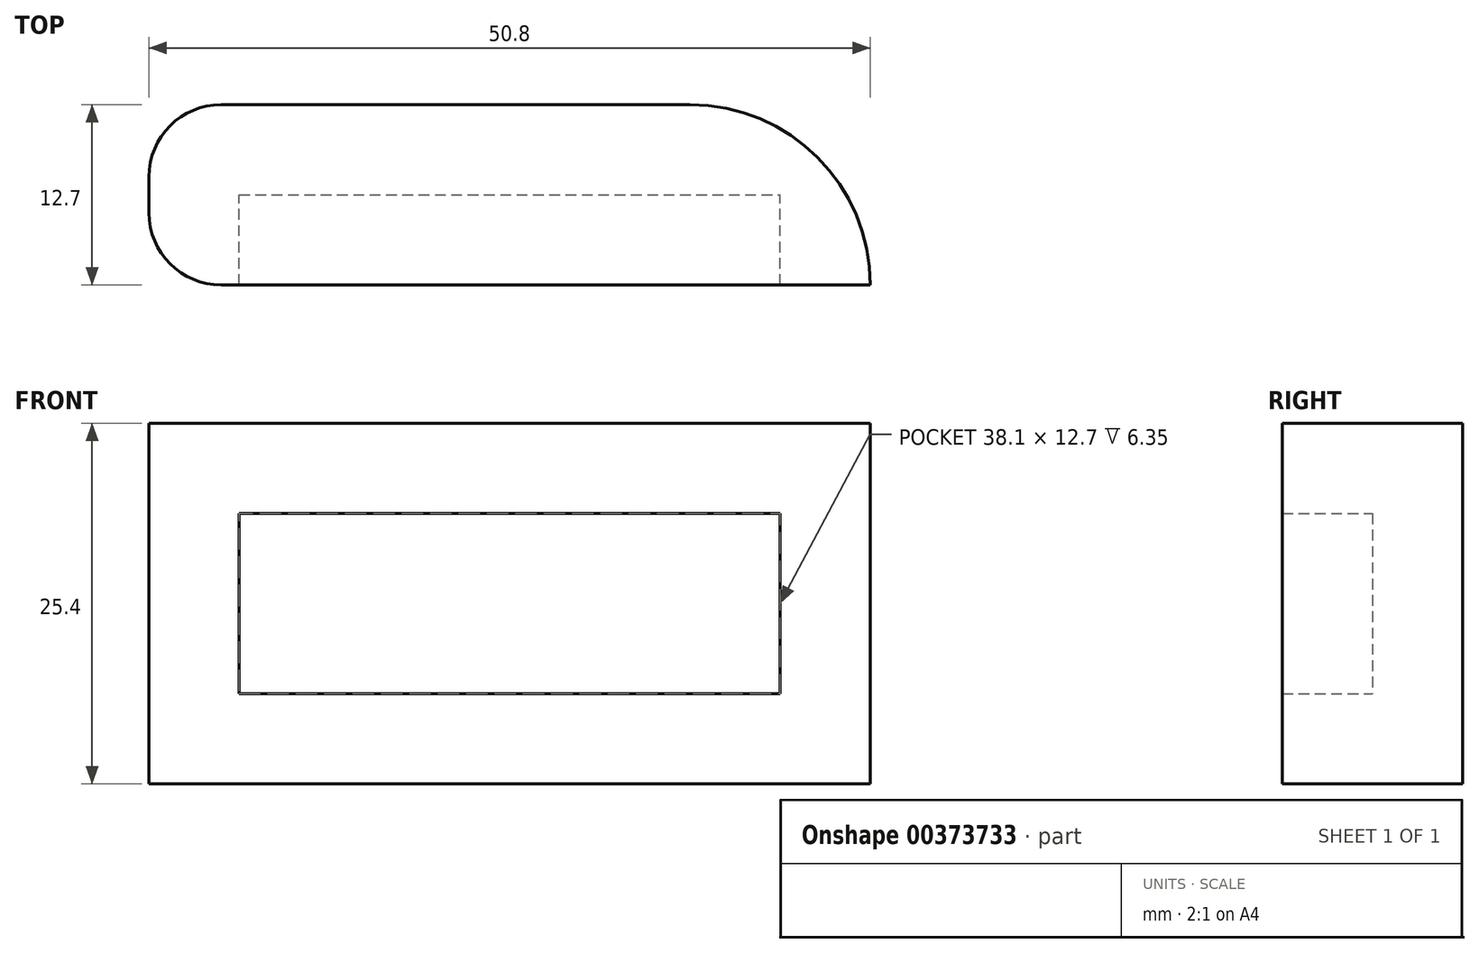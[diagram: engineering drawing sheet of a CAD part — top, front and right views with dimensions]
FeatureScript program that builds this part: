
annotation { "Feature Type Name" : "Feature", "Feature Type Description" : "" }
export const myFeature = defineFeature(function(context is Context, id is Id, definition is map)
    precondition{}
    {
        {
            var Q0;
            Q0=qCreatedBy(makeId("Front.planeOp"),FACE);
            var sketch = newSketch(context, id + "F0", { "sketchPlane" : qUnion([Q0])});
            skLineSegment(sketch, "E0.bottom", {"start": v(0, 0) * mm, "end": v(50.8, 0) * mm});
            skLineSegment(sketch, "E0.top", {"start": v(0, 25.4) * mm, "end": v(50.8, 25.4) * mm});
            skLineSegment(sketch, "E0.left", {"start": v(0, 0) * mm, "end": v(0, 25.4) * mm});
            skLineSegment(sketch, "E0.right", {"start": v(50.8, 0) * mm, "end": v(50.8, 25.4) * mm});
            skSolve(sketch);
        }
        {
            var Q0;
            Q0 = qSketchRegion(id + "F0", true);
            extrude(context, id + "F1", {"entities" : qUnion([Q0]), "depth" : 12.7 * mm});
        }
        {
            var Q0;
            Q0=makeQuery(id+"F1.opExtrude","CAP_EDGE",EDGE,{"disambiguationData":[OSD([sQuery(id+"F0.wireOp",EDGE,"E0.left")])],"isStart":true});
            var Q1;
            Q1=makeQuery(id+"F1.opExtrude","CAP_EDGE",EDGE,{"disambiguationData":[OSD([sQuery(id+"F0.wireOp",EDGE,"E0.left")])],"isStart":false});
            fillet(context, id + "F2", {"entities" : qUnion([Q0, Q1]), "radius" : 5.08 * mm, "tangentPropagation" : true, "allowEdgeOverflow" : false});
        }
        {
            var Q0;
            Q0=makeQuery(id+"F1.opExtrude","CAP_FACE",FACE,{"disambiguationData":[OSD([sQuery(id+"F0.wireOp",EDGE,"E0.bottom"),sQuery(id+"F0.wireOp",EDGE,"E0.top"),sQuery(id+"F0.wireOp",EDGE,"E0.left"),sQuery(id+"F0.wireOp",EDGE,"E0.right")])],"isStart":false});
            shell(context, id + "F3", {"entities" : qUnion([Q0]), "thickness" : 6.35 * mm});
        }
        {
            var Q0;
            Q0=makeQuery(id+"F1.opExtrude","CAP_EDGE",EDGE,{"disambiguationData":[OSD([sQuery(id+"F0.wireOp",EDGE,"E0.right")])],"isStart":true});
            fillet(context, id + "F4", {"entities" : qUnion([Q0]), "radius" : 12.7 * mm, "tangentPropagation" : true, "allowEdgeOverflow" : false});
        }
    });
